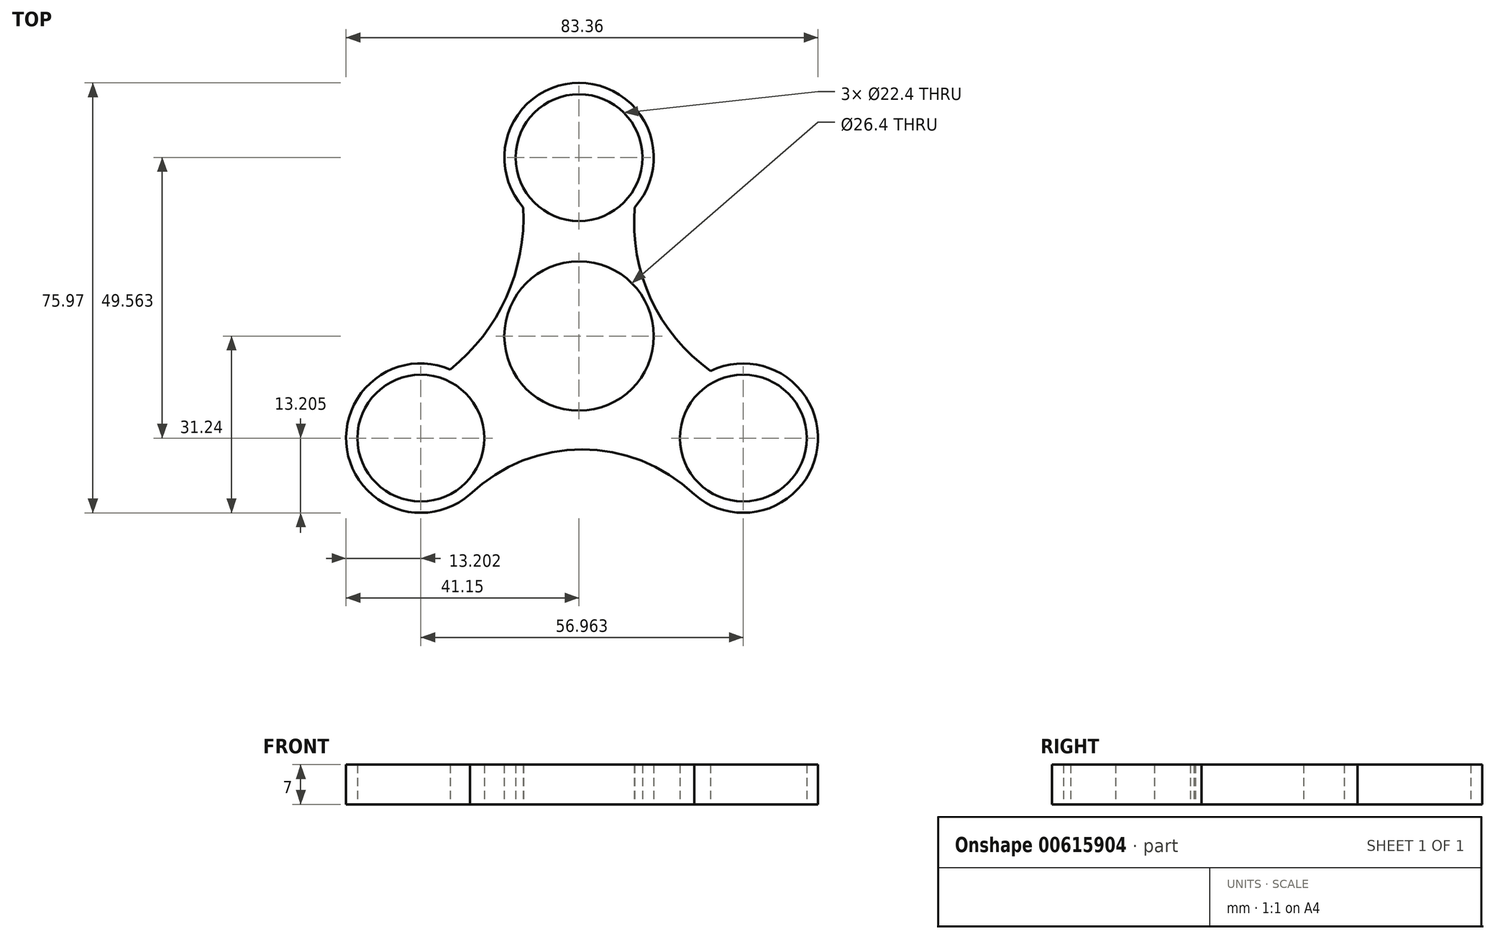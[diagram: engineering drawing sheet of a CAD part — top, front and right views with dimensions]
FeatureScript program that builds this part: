
annotation { "Feature Type Name" : "Feature", "Feature Type Description" : "" }
export const myFeature = defineFeature(function(context is Context, id is Id, definition is map)
    precondition{}
    {
        {
            var Q0;
            Q0=qCreatedBy(makeId("Top.planeOp"),FACE);
            var sketch = newSketch(context, id + "F0", { "sketchPlane" : qUnion([Q0])});
            skCircle(sketch, "E0", {"center": v(0, 0) * mm, "radius": 11.2 * mm});
            skCircle(sketch, "E1", {"center": v(0, 0) * mm, "radius": 13.2 * mm});
            skCircle(sketch, "E2", {"center": v(0, 31.53) * mm, "radius": 11.2 * mm});
            skArc(sketch, "E3", {"start": v(9.84, 22.73) * mm, "mid": v(0, 44.73) * mm, "end": v(-9.84, 22.73) * mm});
            skCircle(sketch, "E4", {"center": v(29.01, -18.04) * mm, "radius": 11.2 * mm});
            skCircle(sketch, "E5", {"center": v(-27.95, -18.04) * mm, "radius": 11.2 * mm});
            skArc(sketch, "E6", {"start": v(20.34, -27.99) * mm, "mid": v(42.1, -19.78) * mm, "end": v(23.25, -6.16) * mm});
            skArc(sketch, "E7", {"start": v(-22.73, -5.9) * mm, "mid": v(-12.84, 6.86) * mm, "end": v(-9.84, 22.73) * mm});
            skArc(sketch, "E8", {"start": v(9.84, 22.73) * mm, "mid": v(12.7, 6.5) * mm, "end": v(23.25, -6.16) * mm});
            skArc(sketch, "E9", {"start": v(-22.73, -5.9) * mm, "mid": v(-40.92, -20.5) * mm, "end": v(-18.65, -27.4) * mm});
            skArc(sketch, "E10", {"start": v(20.34, -27.99) * mm, "mid": v(0.53, -20.03) * mm, "end": v(-19.28, -27.99) * mm});
            skSolve(sketch);
        }
        {
            var Q0;
            Q0=makeQuery(id+"F0.imprint","IMPRINT",FACE,{"disambiguationData":[TD([[makeQuery(id+"F0.imprint","IMPRINT",EDGE,{"derivedFrom":sQuery(id+"F0.wireOp",EDGE,"E1")}),-1.0]])]});
            extrude(context, id + "F1", {"entities" : qUnion([Q0]), "depth" : 7 * mm, "offsetDistance" : 25 * mm});
        }
    });
